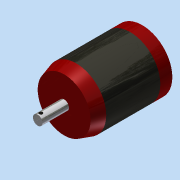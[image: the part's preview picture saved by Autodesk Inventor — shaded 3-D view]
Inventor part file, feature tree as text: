
AUTODESK INVENTOR PART (.ipt)
format: ipt  version: 2015 (Build 190159000, 159)  size: 117,760 bytes
history: native  units: in
note: dims shown in document units (in); Inventor stores cm internally (conversion verified against a paired STEP export)
features: extrude x3, sketch x3, plane x2, split x2, chamfer x1, projected_geometry x1
ambient origin geometry x8: Origin, YZ Plane, XZ Plane, XY Plane, X Axis, Y Axis, Z Axis, Center Point
bodies: Solid1 (feature_tree)
feature tree (12):
  extrude  "Extrusion1"  Depth=2.5591in TaperAngle=0.0deg
  extrude  "Extrusion2"  Depth=0.8661in TaperAngle=0.0deg
  plane  "Work Plane1"
  plane  "Work Plane2"
  split  "Split1"
  split  "Split2"
  chamfer  "Chamfer1"  [1 undecoded]
  extrude  "Extrusion3"  Depth=0.3937in TaperAngle=45.0deg
  sketch  "Sketch2"  dims[d0=1.9685in d1=2.5591in d2=0.0in]
  sketch  "Sketch3"  dims[d3=0.315in d4=0.8661in d5=0.0in]
  sketch  "Sketch4"  dims[d6=-0.3937in d7=-0.3937in d8=0.1181in d9=0.3937in d10=45.0deg d11=0.1181in d12=0.0984in d13=1.0in d14=0.0in]
  projected_geometry  "Projected Loop1"
note: 1 required parameter value undecoded (feature->parameter linkage not recoverable at this tier; creation-order binding heuristic only, values carry confidence <= 0.55)
